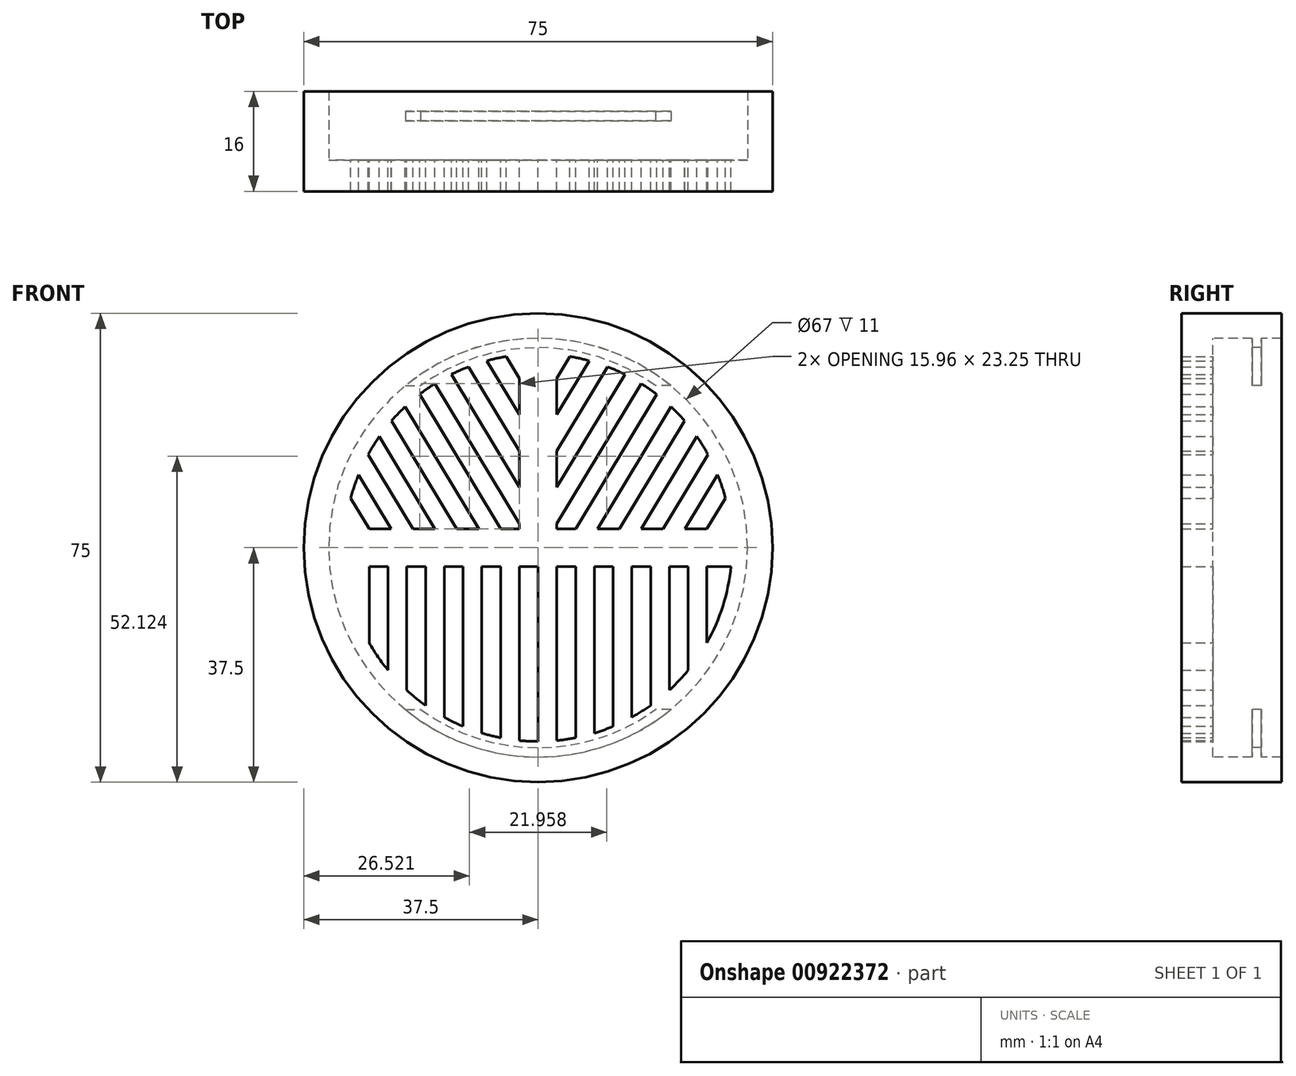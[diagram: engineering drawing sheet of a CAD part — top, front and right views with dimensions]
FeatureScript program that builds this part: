
annotation { "Feature Type Name" : "Feature", "Feature Type Description" : "" }
export const myFeature = defineFeature(function(context is Context, id is Id, definition is map)
    precondition{}
    {
        {
            var Q0;
            Q0=qCreatedBy(makeId("Front.planeOp"),FACE);
            var sketch = newSketch(context, id + "F0", { "sketchPlane" : qUnion([Q0])});
            skCircle(sketch, "E0", {"center": v(0, 0) * mm, "radius": 37.5 * mm});
            skCircle(sketch, "E1", {"center": v(0, 0) * mm, "radius": 31 * mm});
            skLineSegment(sketch, "E2.right", {"start": v(-3, 3) * mm, "end": v(-3, 30.85) * mm});
            skPoint(sketch, "E3.orphan", {"position": v(-3, -30.85) * mm});
            skPoint(sketch, "E4.orphan", {"position": v(3, -30.85) * mm});
            skLineSegment(sketch, "E5.left", {"start": v(-3, -3) * mm, "end": v(-3, -30.85) * mm});
            skLineSegment(sketch, "E6.1.0.0", {"start": v(0, -3) * mm, "end": v(0, -31) * mm});
            skLineSegment(sketch, "E6.2.0.0", {"start": v(3, -3) * mm, "end": v(3, -30.85) * mm});
            skLineSegment(sketch, "E6.3.0.0", {"start": v(6, -3) * mm, "end": v(6, -30.41) * mm});
            skLineSegment(sketch, "E6.4.0.0", {"start": v(9, -3) * mm, "end": v(9, -29.66) * mm});
            skLineSegment(sketch, "E6.5.0.0", {"start": v(12, -3) * mm, "end": v(12, -28.58) * mm});
            skLineSegment(sketch, "E6.6.0.0", {"start": v(15, -3) * mm, "end": v(15, -27.13) * mm});
            skLineSegment(sketch, "E6.7.0.0", {"start": v(18, -3) * mm, "end": v(18, -25.24) * mm});
            skLineSegment(sketch, "E6.8.0.0", {"start": v(21, -3) * mm, "end": v(21, -22.8) * mm});
            skLineSegment(sketch, "E6.9.0.0", {"start": v(24, -3) * mm, "end": v(24, -19.62) * mm});
            skLineSegment(sketch, "E6.10.0.0", {"start": v(27, -3) * mm, "end": v(27, -15.23) * mm});
            skLineSegment(sketch, "E6.direction1", {"start": v(-3, -31.13) * mm, "end": v(0, -31.13) * mm, "construction": true});
            skPoint(sketch, "E7.orphan", {"position": v(6, -31.13) * mm});
            skPoint(sketch, "E8.orphan", {"position": v(3, -31.13) * mm});
            skPoint(sketch, "E9.orphan", {"position": v(9, -31.13) * mm});
            skLineSegment(sketch, "E10.trimOffspring", {"start": v(12, -31.13) * mm, "end": v(12, -35.53) * mm});
            skPoint(sketch, "E11.orphan", {"position": v(18, -31.13) * mm});
            skPoint(sketch, "E12.orphan", {"position": v(30, -31.13) * mm});
            skLineSegment(sketch, "E13.1.0.0", {"start": v(-6, -3) * mm, "end": v(-6, -30.41) * mm});
            skLineSegment(sketch, "E13.2.0.0", {"start": v(-9, -3) * mm, "end": v(-9, -29.66) * mm});
            skLineSegment(sketch, "E13.3.0.0", {"start": v(-12, -3) * mm, "end": v(-12, -28.58) * mm});
            skLineSegment(sketch, "E13.4.0.0", {"start": v(-15, -3) * mm, "end": v(-15, -27.13) * mm});
            skLineSegment(sketch, "E13.5.0.0", {"start": v(-18, -3) * mm, "end": v(-18, -25.24) * mm});
            skLineSegment(sketch, "E13.6.0.0", {"start": v(-21, -3) * mm, "end": v(-21, -22.8) * mm});
            skLineSegment(sketch, "E13.7.0.0", {"start": v(-24, -3) * mm, "end": v(-24, -19.62) * mm});
            skLineSegment(sketch, "E13.8.0.0", {"start": v(-27, -3) * mm, "end": v(-27, -15.23) * mm});
            skLineSegment(sketch, "E13.direction1", {"start": v(-3, -31.13) * mm, "end": v(-6, -31.13) * mm, "construction": true});
            skPoint(sketch, "E14.orphan", {"position": v(-9, -31.13) * mm});
            skPoint(sketch, "E15.orphan", {"position": v(-12, -31.13) * mm});
            skLineSegment(sketch, "E16", {"start": v(-6, 3) * mm, "end": v(-18.96, 24.53) * mm});
            skLineSegment(sketch, "E17.0", {"start": v(-3, 3.83) * mm, "end": v(-16.5, 26.25) * mm});
            skLineSegment(sketch, "E18.0", {"start": v(-3, 9.65) * mm, "end": v(-13.88, 27.72) * mm});
            skLineSegment(sketch, "E19.0", {"start": v(-3, 15.47) * mm, "end": v(-11.11, 28.94) * mm});
            skLineSegment(sketch, "E20.0", {"start": v(-9.5, 3) * mm, "end": v(-21.27, 22.55) * mm});
            skLineSegment(sketch, "E21.0", {"start": v(-13, 3) * mm, "end": v(-23.42, 20.3) * mm});
            skLineSegment(sketch, "E22.0", {"start": v(-16.5, 3) * mm, "end": v(-25.4, 17.77) * mm});
            skLineSegment(sketch, "E23.0", {"start": v(-20, 3) * mm, "end": v(-27.18, 14.91) * mm});
            skLineSegment(sketch, "E24.0", {"start": v(-23.5, 3) * mm, "end": v(-28.72, 11.66) * mm});
            skLineSegment(sketch, "E25.trimOffspring", {"start": v(-27, 3) * mm, "end": v(-29.97, 7.92) * mm});
            skLineSegment(sketch, "E26.trimOffspring", {"start": v(-3, 21.28) * mm, "end": v(-8.19, 29.9) * mm});
            skLineSegment(sketch, "E27.0", {"start": v(-3, 27.1) * mm, "end": v(-5.1, 30.58) * mm});
            skLineSegment(sketch, "E28", {"start": v(3, 3) * mm, "end": v(3, 30.85) * mm});
            skLineSegment(sketch, "E29", {"start": v(-3, 3) * mm, "end": v(-30.85, 3) * mm});
            skLineSegment(sketch, "E30", {"start": v(3, 3) * mm, "end": v(30.85, 3) * mm});
            skLineSegment(sketch, "E31", {"start": v(-30.85, -3) * mm, "end": v(30.85, -3) * mm});
            skLineSegment(sketch, "E32.MirrorCS", {"start": v(3, 27.1) * mm, "end": v(5.1, 30.58) * mm});
            skLineSegment(sketch, "E33.MirrorCS", {"start": v(3, 21.28) * mm, "end": v(8.19, 29.9) * mm});
            skLineSegment(sketch, "E34.MirrorCS", {"start": v(3, 15.47) * mm, "end": v(11.11, 28.94) * mm});
            skLineSegment(sketch, "E35.MirrorCS", {"start": v(3, 9.65) * mm, "end": v(13.88, 27.72) * mm});
            skLineSegment(sketch, "E36.MirrorCS", {"start": v(3, 3.83) * mm, "end": v(16.5, 26.25) * mm});
            skLineSegment(sketch, "E37.MirrorCS", {"start": v(6, 3) * mm, "end": v(18.96, 24.53) * mm});
            skLineSegment(sketch, "E38.MirrorCS", {"start": v(9.5, 3) * mm, "end": v(21.27, 22.55) * mm});
            skLineSegment(sketch, "E39.MirrorCS", {"start": v(13, 3) * mm, "end": v(23.42, 20.3) * mm});
            skLineSegment(sketch, "E40.MirrorCS", {"start": v(16.5, 3) * mm, "end": v(25.4, 17.77) * mm});
            skLineSegment(sketch, "E41.MirrorCS", {"start": v(20, 3) * mm, "end": v(27.18, 14.91) * mm});
            skLineSegment(sketch, "E42.MirrorCS", {"start": v(23.5, 3) * mm, "end": v(28.72, 11.66) * mm});
            skLineSegment(sketch, "E43.MirrorCS", {"start": v(27, 3) * mm, "end": v(29.97, 7.92) * mm});
            skSolve(sketch);
        }
        {
            var Q0;
            {var subQ19=sQuery(id+"F0.wireOp",EDGE,"E28");Q0=makeQuery(id+"F0.imprint","IMPRINT",FACE,{"disambiguationData":[TD([[makeQuery(id+"F0.imprint","IMPRINT",EDGE,{"derivedFrom":subQ19}),1.0]])]});}
            var Q1;
            Q1=makeQuery(id+"F0.imprint","IMPRINT",FACE,{"disambiguationData":[TD([[makeQuery(id+"F0.imprint","IMPRINT",EDGE,{"derivedFrom":sQuery(id+"F0.wireOp",EDGE,"E0")}),1.0]])]});
            var Q2;
            {var subQ3=sQuery(id+"F0.wireOp",EDGE,"E27.0");Q2=makeQuery(id+"F0.imprint","IMPRINT",FACE,{"disambiguationData":[TD([[makeQuery(id+"F0.imprint","IMPRINT",EDGE,{"derivedFrom":subQ3}),-1.0]])]});}
            var Q3;
            {var subQ0=sQuery(id+"F0.wireOp",EDGE,"E19.0");Q3=makeQuery(id+"F0.imprint","IMPRINT",FACE,{"disambiguationData":[TD([[makeQuery(id+"F0.imprint","IMPRINT",EDGE,{"derivedFrom":subQ0}),-1.0]])]});}
            var Q4;
            {var subQ0=sQuery(id+"F0.wireOp",EDGE,"E17.0");Q4=makeQuery(id+"F0.imprint","IMPRINT",FACE,{"disambiguationData":[TD([[makeQuery(id+"F0.imprint","IMPRINT",EDGE,{"derivedFrom":subQ0}),-1.0]])]});}
            var Q5;
            {var subQ0=sQuery(id+"F0.wireOp",EDGE,"E16");Q5=makeQuery(id+"F0.imprint","IMPRINT",FACE,{"disambiguationData":[TD([[makeQuery(id+"F0.imprint","IMPRINT",EDGE,{"derivedFrom":subQ0}),1.0]])]});}
            var Q6;
            {var subQ0=sQuery(id+"F0.wireOp",EDGE,"E21.0");Q6=makeQuery(id+"F0.imprint","IMPRINT",FACE,{"disambiguationData":[TD([[makeQuery(id+"F0.imprint","IMPRINT",EDGE,{"derivedFrom":subQ0}),1.0]])]});}
            var Q7;
            {var subQ0=sQuery(id+"F0.wireOp",EDGE,"E23.0");Q7=makeQuery(id+"F0.imprint","IMPRINT",FACE,{"disambiguationData":[TD([[makeQuery(id+"F0.imprint","IMPRINT",EDGE,{"derivedFrom":subQ0}),1.0]])]});}
            var Q8;
            {var subQ0=sQuery(id+"F0.wireOp",EDGE,"E25.trimOffspring");Q8=makeQuery(id+"F0.imprint","IMPRINT",FACE,{"disambiguationData":[TD([[makeQuery(id+"F0.imprint","IMPRINT",EDGE,{"derivedFrom":subQ0}),1.0]])]});}
            var Q9;
            {var subQ0=sQuery(id+"F0.wireOp",EDGE,"E5.left");Q9=makeQuery(id+"F0.imprint","IMPRINT",FACE,{"disambiguationData":[TD([[makeQuery(id+"F0.imprint","IMPRINT",EDGE,{"derivedFrom":subQ0}),-1.0]])]});}
            var Q10;
            {var subQ0=sQuery(id+"F0.wireOp",EDGE,"E13.2.0.0");Q10=makeQuery(id+"F0.imprint","IMPRINT",FACE,{"disambiguationData":[TD([[makeQuery(id+"F0.imprint","IMPRINT",EDGE,{"derivedFrom":subQ0}),-1.0]])]});}
            var Q11;
            {var subQ0=sQuery(id+"F0.wireOp",EDGE,"E13.4.0.0");Q11=makeQuery(id+"F0.imprint","IMPRINT",FACE,{"disambiguationData":[TD([[makeQuery(id+"F0.imprint","IMPRINT",EDGE,{"derivedFrom":subQ0}),-1.0]])]});}
            var Q12;
            {var subQ0=sQuery(id+"F0.wireOp",EDGE,"E13.6.0.0");Q12=makeQuery(id+"F0.imprint","IMPRINT",FACE,{"disambiguationData":[TD([[makeQuery(id+"F0.imprint","IMPRINT",EDGE,{"derivedFrom":subQ0}),-1.0]])]});}
            var Q13;
            {var subQ0=sQuery(id+"F0.wireOp",EDGE,"E13.8.0.0");Q13=makeQuery(id+"F0.imprint","IMPRINT",FACE,{"disambiguationData":[TD([[makeQuery(id+"F0.imprint","IMPRINT",EDGE,{"derivedFrom":subQ0}),-1.0]])]});}
            var Q14;
            {var subQ0=sQuery(id+"F0.wireOp",EDGE,"E6.1.0.0");Q14=makeQuery(id+"F0.imprint","IMPRINT",FACE,{"disambiguationData":[TD([[makeQuery(id+"F0.imprint","IMPRINT",EDGE,{"derivedFrom":subQ0}),1.0]])]});}
            var Q15;
            {var subQ0=sQuery(id+"F0.wireOp",EDGE,"E6.3.0.0");Q15=makeQuery(id+"F0.imprint","IMPRINT",FACE,{"disambiguationData":[TD([[makeQuery(id+"F0.imprint","IMPRINT",EDGE,{"derivedFrom":subQ0}),1.0]])]});}
            var Q16;
            {var subQ0=sQuery(id+"F0.wireOp",EDGE,"E6.5.0.0");Q16=makeQuery(id+"F0.imprint","IMPRINT",FACE,{"disambiguationData":[TD([[makeQuery(id+"F0.imprint","IMPRINT",EDGE,{"derivedFrom":subQ0}),1.0]])]});}
            var Q17;
            {var subQ0=sQuery(id+"F0.wireOp",EDGE,"E6.7.0.0");Q17=makeQuery(id+"F0.imprint","IMPRINT",FACE,{"disambiguationData":[TD([[makeQuery(id+"F0.imprint","IMPRINT",EDGE,{"derivedFrom":subQ0}),1.0]])]});}
            var Q18;
            {var subQ0=sQuery(id+"F0.wireOp",EDGE,"E6.9.0.0");Q18=makeQuery(id+"F0.imprint","IMPRINT",FACE,{"disambiguationData":[TD([[makeQuery(id+"F0.imprint","IMPRINT",EDGE,{"derivedFrom":subQ0}),1.0]])]});}
            var Q19;
            {var subQ3=sQuery(id+"F0.wireOp",EDGE,"E32.MirrorCS");Q19=makeQuery(id+"F0.imprint","IMPRINT",FACE,{"disambiguationData":[TD([[makeQuery(id+"F0.imprint","IMPRINT",EDGE,{"derivedFrom":subQ3}),1.0]])]});}
            var Q20;
            {var subQ0=sQuery(id+"F0.wireOp",EDGE,"E33.MirrorCS");Q20=makeQuery(id+"F0.imprint","IMPRINT",FACE,{"disambiguationData":[TD([[makeQuery(id+"F0.imprint","IMPRINT",EDGE,{"derivedFrom":subQ0}),-1.0]])]});}
            var Q21;
            {var subQ0=sQuery(id+"F0.wireOp",EDGE,"E35.MirrorCS");Q21=makeQuery(id+"F0.imprint","IMPRINT",FACE,{"disambiguationData":[TD([[makeQuery(id+"F0.imprint","IMPRINT",EDGE,{"derivedFrom":subQ0}),-1.0]])]});}
            var Q22;
            {var subQ0=sQuery(id+"F0.wireOp",EDGE,"E37.MirrorCS");Q22=makeQuery(id+"F0.imprint","IMPRINT",FACE,{"disambiguationData":[TD([[makeQuery(id+"F0.imprint","IMPRINT",EDGE,{"derivedFrom":subQ0}),-1.0]])]});}
            var Q23;
            {var subQ0=sQuery(id+"F0.wireOp",EDGE,"E39.MirrorCS");Q23=makeQuery(id+"F0.imprint","IMPRINT",FACE,{"disambiguationData":[TD([[makeQuery(id+"F0.imprint","IMPRINT",EDGE,{"derivedFrom":subQ0}),-1.0]])]});}
            var Q24;
            {var subQ0=sQuery(id+"F0.wireOp",EDGE,"E41.MirrorCS");Q24=makeQuery(id+"F0.imprint","IMPRINT",FACE,{"disambiguationData":[TD([[makeQuery(id+"F0.imprint","IMPRINT",EDGE,{"derivedFrom":subQ0}),-1.0]])]});}
            var Q25;
            {var subQ3=sQuery(id+"F0.wireOp",EDGE,"E43.MirrorCS");Q25=makeQuery(id+"F0.imprint","IMPRINT",FACE,{"disambiguationData":[TD([[makeQuery(id+"F0.imprint","IMPRINT",EDGE,{"derivedFrom":subQ3}),-1.0]])]});}
            extrude(context, id + "F1", {"entities" : qUnion([Q0, Q1, Q2, Q3, Q4, Q5, Q6, Q7, Q8, Q9, Q10, Q11, Q12, Q13, Q14, Q15, Q16, Q17, Q18, Q19, Q20, Q21, Q22, Q23, Q24, Q25]), "depth" : 5 * mm, "offsetDistance" : 25 * mm});
        }
        {
            var Q0;
            Q0=qCreatedBy(makeId("Front.planeOp"),FACE);
            var sketch = newSketch(context, id + "F2", { "sketchPlane" : qUnion([Q0])});
            skCircle(sketch, "E44", {"center": v(0, 0) * mm, "radius": 33.5 * mm});
            skCircle(sketch, "E45", {"center": v(0, 0) * mm, "radius": 37.5 * mm});
            skSolve(sketch);
        }
        {
            var Q0;
            Q0=makeQuery(id+"F2.imprint","IMPRINT",FACE,{"disambiguationData":[TD([[makeQuery(id+"F2.imprint","IMPRINT",EDGE,{"derivedFrom":sQuery(id+"F2.wireOp",EDGE,"E44")}),-1.0]])]});
            extrude(context, id + "F3", {"entities" : qUnion([Q0]), "operationType" : NewBodyOperationType.ADD, "oppositeDirection" : true, "depth" : 11 * mm, "offsetDistance" : 25 * mm});
        }
        {
            var Q0;
            Q0=qCreatedBy(makeId("Front.planeOp"),FACE);
            var sketch = newSketch(context, id + "F4", { "sketchPlane" : qUnion([Q0])});
            skArc(sketch, "E46", {"start": v(21.24, 25.9) * mm, "mid": v(0, 33.5) * mm, "end": v(-21.23, 25.9) * mm});
            skArc(sketch, "E47.0", {"start": v(18.79, 25.9) * mm, "mid": v(0, 32) * mm, "end": v(-18.78, 25.9) * mm});
            skLineSegment(sketch, "E48", {"start": v(-21.23, 25.9) * mm, "end": v(-18.78, 25.9) * mm});
            skLineSegment(sketch, "E49", {"start": v(21.24, 25.9) * mm, "end": v(18.79, 25.9) * mm});
            skLineSegment(sketch, "E50.MirrorCS", {"start": v(-21.23, -25.9) * mm, "end": v(-18.78, -25.9) * mm});
            skArc(sketch, "E51.MirrorCS", {"start": v(21.24, -25.9) * mm, "mid": v(0, -33.5) * mm, "end": v(-21.23, -25.9) * mm});
            skArc(sketch, "E52.MirrorCS", {"start": v(18.79, -25.9) * mm, "mid": v(0, -32) * mm, "end": v(-18.78, -25.9) * mm});
            skLineSegment(sketch, "E53.MirrorCS", {"start": v(21.24, -25.9) * mm, "end": v(18.79, -25.9) * mm});
            skSolve(sketch);
        }
        {
            var Q0;
            Q0=makeQuery(id+"F4.imprint","IMPRINT",FACE,{"disambiguationData":[TD([[makeQuery(id+"F4.imprint","IMPRINT",EDGE,{"derivedFrom":sQuery(id+"F4.wireOp",EDGE,"E47.0")}),-1.0]])]});
            var Q1;
            Q1=makeQuery(id+"F4.imprint","IMPRINT",FACE,{"disambiguationData":[TD([[makeQuery(id+"F4.imprint","IMPRINT",EDGE,{"derivedFrom":sQuery(id+"F4.wireOp",EDGE,"E50.MirrorCS")}),-1.0]])]});
            extrude(context, id + "F5", {"entities" : qUnion([Q0, Q1]), "operationType" : NewBodyOperationType.ADD, "oppositeDirection" : true, "depth" : 7.8 * mm, "offsetDistance" : 25 * mm});
        }
        {
            var Q0;
            Q0=makeQuery(id+"F4.imprint","IMPRINT",FACE,{"disambiguationData":[TD([[makeQuery(id+"F4.imprint","IMPRINT",EDGE,{"derivedFrom":sQuery(id+"F4.wireOp",EDGE,"E47.0")}),-1.0]])]});
            var Q1;
            Q1=makeQuery(id+"F4.imprint","IMPRINT",FACE,{"disambiguationData":[TD([[makeQuery(id+"F4.imprint","IMPRINT",EDGE,{"derivedFrom":sQuery(id+"F4.wireOp",EDGE,"E50.MirrorCS")}),-1.0]])]});
            extrude(context, id + "F6", {"entities" : qUnion([Q0, Q1]), "operationType" : NewBodyOperationType.REMOVE, "oppositeDirection" : true, "depth" : 6.3 * mm, "offsetDistance" : 25 * mm});
        }
    });
